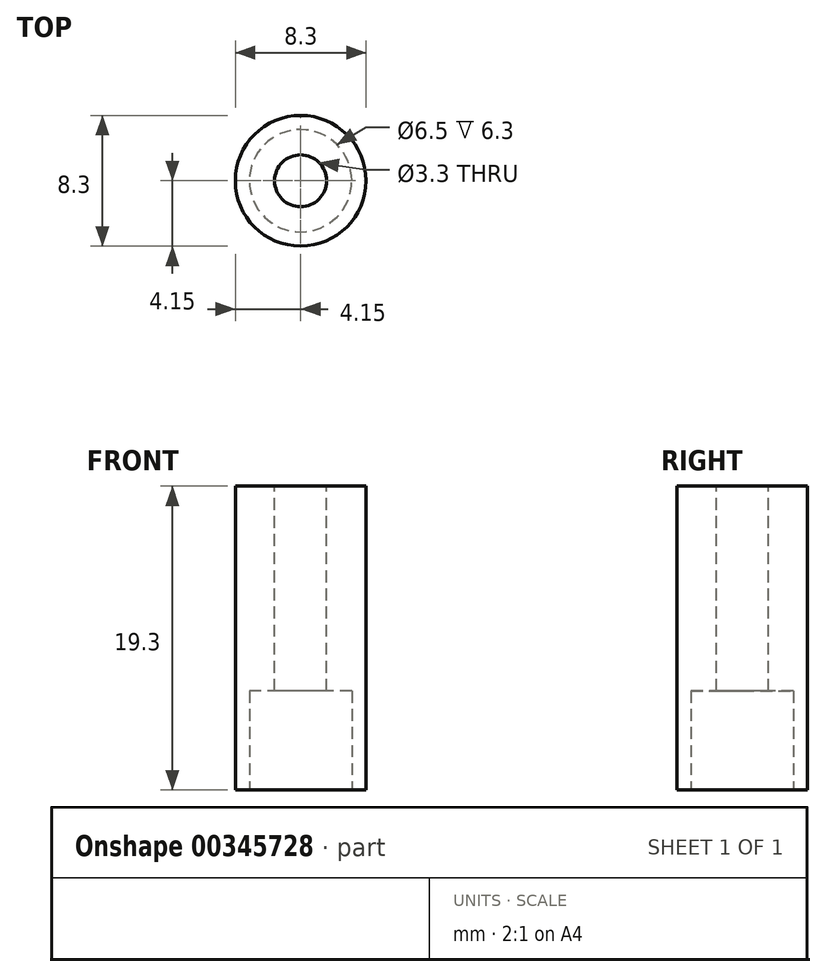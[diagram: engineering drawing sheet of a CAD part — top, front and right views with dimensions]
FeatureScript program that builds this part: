
annotation { "Feature Type Name" : "Feature", "Feature Type Description" : "" }
export const myFeature = defineFeature(function(context is Context, id is Id, definition is map)
    precondition{}
    {
        {
            var Q0;
            Q0=qCreatedBy(makeId("Top.planeOp"),FACE);
            var sketch = newSketch(context, id + "F0", { "sketchPlane" : qUnion([Q0])});
            skCircle(sketch, "E0", {"center": v(0, 0) * mm, "radius": 3.25 * mm});
            skCircle(sketch, "E1", {"center": v(0, 0) * mm, "radius": 4.15 * mm});
            skSolve(sketch);
        }
        {
            var Q0;
            Q0 = qSketchRegion(id + "F0", true);
            extrude(context, id + "F1", {"entities" : qUnion([Q0]), "depth" : 6.3 * mm});
        }
        {
            var Q0;
            Q0=makeQuery(id+"F1.opExtrude","CAP_FACE",FACE,{"disambiguationData":[OSD([sQuery(id+"F0.wireOp",EDGE,"E0"),sQuery(id+"F0.wireOp",EDGE,"E1")])],"isStart":false});
            var sketch = newSketch(context, id + "F2", { "sketchPlane" : qUnion([Q0])});
            skCircle(sketch, "E2", {"center": v(0, 0) * mm, "radius": 4.15 * mm});
            skSolve(sketch);
        }
        {
            var Q0;
            Q0 = qSketchRegion(id + "F2", true);
            extrude(context, id + "F3", {"entities" : qUnion([Q0]), "operationType" : NewBodyOperationType.ADD, "depth" : 1 * mm});
        }
        {
            var Q0;
            Q0=makeQuery(id+"F3.opExtrude","CAP_FACE",FACE,{"disambiguationData":[OSD([sQuery(id+"F2.wireOp",EDGE,"E2")])],"isStart":false});
            var sketch = newSketch(context, id + "F4", { "sketchPlane" : qUnion([Q0])});
            skCircle(sketch, "E3", {"center": v(0, 0) * mm, "radius": 1.65 * mm});
            skSolve(sketch);
        }
        {
            var Q0;
            Q0 = qSketchRegion(id + "F4", true);
            extrude(context, id + "F5", {"entities" : qUnion([Q0]), "operationType" : NewBodyOperationType.REMOVE, "endBound" : BoundingType.UP_TO_NEXT, "oppositeDirection" : true, "depth" : 25 * mm});
        }
        {
            var Q0;
            Q0=makeQuery(id+"F3.opExtrude","CAP_FACE",FACE,{"disambiguationData":[OSD([sQuery(id+"F2.wireOp",EDGE,"E2")])],"isStart":false});
            var sketch = newSketch(context, id + "F6", { "sketchPlane" : qUnion([Q0])});
            skCircle(sketch, "E4", {"center": v(0, 0) * mm, "radius": 1.65 * mm});
            skCircle(sketch, "E5", {"center": v(0, 0) * mm, "radius": 4.15 * mm});
            skSolve(sketch);
        }
        {
            var Q0;
            Q0 = qSketchRegion(id + "F6", true);
            extrude(context, id + "F7", {"entities" : qUnion([Q0]), "operationType" : NewBodyOperationType.ADD, "depth" : 12 * mm});
        }
    });
